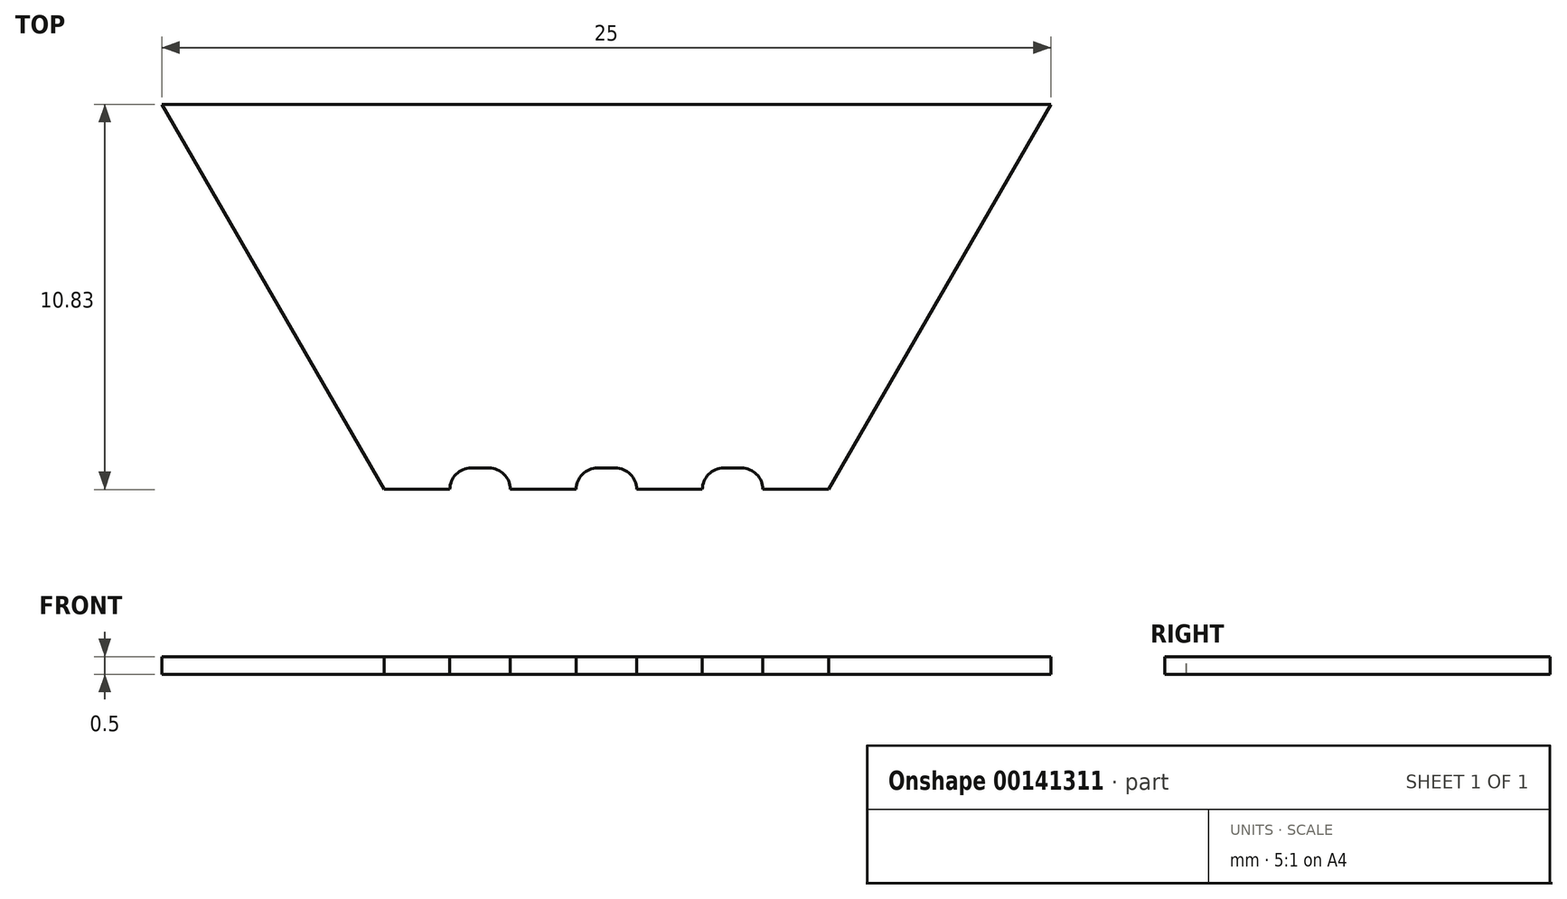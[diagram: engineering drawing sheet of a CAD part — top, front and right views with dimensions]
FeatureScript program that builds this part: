
annotation { "Feature Type Name" : "Feature", "Feature Type Description" : "" }
export const myFeature = defineFeature(function(context is Context, id is Id, definition is map)
    precondition{}
    {
        {
            var Q0;
            Q0=qCreatedBy(makeId("Top.planeOp"),FACE);
            var sketch = newSketch(context, id + "F0", { "sketchPlane" : qUnion([Q0])});
            skCircle(sketch, "E0.cCircle", {"center": v(0, 0) * mm, "radius": 12.5 * mm, "construction": true});
            skLineSegment(sketch, "E0.0", {"start": v(12.5, 0) * mm, "end": v(6.25, -10.83) * mm});
            skLineSegment(sketch, "E0.1", {"start": v(6.25, -10.83) * mm, "end": v(-6.25, -10.83) * mm});
            skLineSegment(sketch, "E0.2", {"start": v(-6.25, -10.83) * mm, "end": v(-12.5, 0) * mm});
            skLineSegment(sketch, "E0.3", {"start": v(-12.5, 0) * mm, "end": v(-6.25, 10.83) * mm});
            skLineSegment(sketch, "E0.4", {"start": v(-6.25, 10.83) * mm, "end": v(6.25, 10.83) * mm});
            skLineSegment(sketch, "E0.5", {"start": v(6.25, 10.83) * mm, "end": v(12.5, 0) * mm});
            skSolve(sketch);
        }
        {
            var Q0;
            Q0=qSketchRegion(id+"F0",true);
            extrude(context, id + "F1", {"entities" : qUnion([Q0]), "depth" : 0.5 * mm});
        }
        {
            var Q0;
            Q0=makeQuery(id+"F1.opExtrude","CAP_FACE",FACE,{"disambiguationData":[OSD([sQuery(id+"F0.wireOp",EDGE,"E0.0"),sQuery(id+"F0.wireOp",EDGE,"E0.1"),sQuery(id+"F0.wireOp",EDGE,"E0.2"),sQuery(id+"F0.wireOp",EDGE,"E0.3"),sQuery(id+"F0.wireOp",EDGE,"E0.4"),sQuery(id+"F0.wireOp",EDGE,"E0.5")])],"isStart":false});
            var sketch = newSketch(context, id + "F2", { "sketchPlane" : qUnion([Q0])});
            skLineSegment(sketch, "E1", {"start": v(3.8, -10.23) * mm, "end": v(3.3, -10.23) * mm});
            skArc(sketch, "E2", {"start": v(3.3, -10.23) * mm, "mid": v(2.88, -10.4) * mm, "end": v(2.7, -10.83) * mm});
            skArc(sketch, "E3", {"start": v(4.4, -10.83) * mm, "mid": v(4.22, -10.4) * mm, "end": v(3.8, -10.23) * mm});
            skLineSegment(sketch, "E4", {"start": v(2.7, -10.83) * mm, "end": v(4.4, -10.83) * mm});
            skPoint(sketch, "E5", {"position": v(-6.25, -10.83) * mm});
            skPoint(sketch, "E6", {"position": v(6.25, -10.83) * mm});
            skLineSegment(sketch, "E7.0", {"start": v(4.4, -10.83) * mm, "end": v(2.7, -10.83) * mm, "construction": true});
            skLineSegment(sketch, "E8", {"start": v(0.25, -10.23) * mm, "end": v(-0.25, -10.23) * mm});
            skArc(sketch, "E9", {"start": v(-0.25, -10.23) * mm, "mid": v(-0.67, -10.4) * mm, "end": v(-0.85, -10.83) * mm});
            skArc(sketch, "E10", {"start": v(0.85, -10.83) * mm, "mid": v(0.67, -10.4) * mm, "end": v(0.25, -10.23) * mm});
            skLineSegment(sketch, "E11", {"start": v(-0.85, -10.83) * mm, "end": v(0.85, -10.83) * mm});
            skLineSegment(sketch, "E12", {"start": v(-3.3, -10.23) * mm, "end": v(-3.8, -10.23) * mm});
            skArc(sketch, "E13", {"start": v(-3.8, -10.23) * mm, "mid": v(-4.22, -10.4) * mm, "end": v(-4.4, -10.83) * mm});
            skArc(sketch, "E14", {"start": v(-2.7, -10.83) * mm, "mid": v(-2.88, -10.4) * mm, "end": v(-3.3, -10.23) * mm});
            skLineSegment(sketch, "E15", {"start": v(-4.4, -10.83) * mm, "end": v(-2.7, -10.83) * mm});
            skLineSegment(sketch, "E16.trimOffspring", {"start": v(0.85, -10.83) * mm, "end": v(-6.25, -10.83) * mm, "construction": true});
            skLineSegment(sketch, "E17", {"start": v(0.85, -10.83) * mm, "end": v(2.7, -10.83) * mm, "construction": true});
            skLineSegment(sketch, "E18", {"start": v(4.4, -10.83) * mm, "end": v(6.25, -10.83) * mm, "construction": true});
            skSolve(sketch);
        }
        {
            var Q0;
            Q0=qSketchRegion(id+"F2",true);
            extrude(context, id + "F3", {"entities" : qUnion([Q0]), "operationType" : NewBodyOperationType.REMOVE, "endBound" : BoundingType.THROUGH_ALL, "oppositeDirection" : true, "depth" : 25 * mm});
        }
        {
            var Q0;
            Q0=makeQuery(id+"F1.opExtrude","CAP_FACE",FACE,{"disambiguationData":[OSD([sQuery(id+"F0.wireOp",EDGE,"E0.0"),sQuery(id+"F0.wireOp",EDGE,"E0.1"),sQuery(id+"F0.wireOp",EDGE,"E0.2"),sQuery(id+"F0.wireOp",EDGE,"E0.3"),sQuery(id+"F0.wireOp",EDGE,"E0.4"),sQuery(id+"F0.wireOp",EDGE,"E0.5")])],"isStart":false});
            var sketch = newSketch(context, id + "F4", { "sketchPlane" : qUnion([Q0])});
            skLineSegment(sketch, "E19", {"start": v(-12.5, 0) * mm, "end": v(12.5, 0) * mm});
            skLineSegment(sketch, "E20", {"start": v(12.5, 0) * mm, "end": v(6.25, 10.83) * mm});
            skLineSegment(sketch, "E21", {"start": v(6.25, 10.83) * mm, "end": v(-6.25, 10.83) * mm});
            skLineSegment(sketch, "E22", {"start": v(-6.25, 10.83) * mm, "end": v(-12.5, 0) * mm});
            skSolve(sketch);
        }
        {
            var Q0;
            Q0 = qSketchRegion(id + "F4", true);
            extrude(context, id + "F5", {"entities" : qUnion([Q0]), "operationType" : NewBodyOperationType.REMOVE, "endBound" : BoundingType.THROUGH_ALL, "oppositeDirection" : true, "depth" : 25 * mm});
        }
    });
